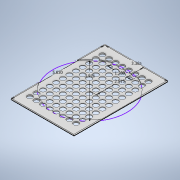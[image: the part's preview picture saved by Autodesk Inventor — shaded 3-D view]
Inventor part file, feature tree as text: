
AUTODESK INVENTOR PART (.ipt)
format: ipt  version: 2020 (Build 240168000, 168)  size: 292,864 bytes
history: native  units: in
note: dims shown in document units (in); Inventor stores cm internally (conversion verified against a paired STEP export)
features: sketch x2, extrude x2, hole x1, pattern_linear x1
ambient origin geometry x8: Origin, YZ Plane, XZ Plane, XY Plane, X Axis, Y Axis, Z Axis, Center Point
bodies: Solid1 (feature_tree)
feature tree (6):
  sketch  "Sketch1"  dims[d0=3.3654in d1=5.0299in]
  extrude  "Extrusion1"  Depth=5.0299in
  extrude  "Extrusion2"  Depth=0.0312in
  hole  "Hole1"  [1 undecoded]
  pattern_linear  "Rectangular Pattern1"  Spacing1=0.0706in  [1 undecoded]
  sketch  "Sketch2"  dims[d2=2.515in d3=3.9764in d4=1.2795in d5=0.0706in d6=0.0in d7=0.0312in d8=0.0in d9=0.2362in d10=0.0in d11=0.2756in d12=0.75in d13=0.438in d14=0.25in d15=0.5635in d16=1.0in d17=0.8108in d18=4.7244in d20=0.3543in d21=3.1496in d23=0.3543in d24=0.2362in d25=0.2362in d26=0.5661in d27=0.4465in]
note: 2 required parameter values undecoded (feature->parameter linkage not recoverable at this tier; creation-order binding heuristic only, values carry confidence <= 0.55)
